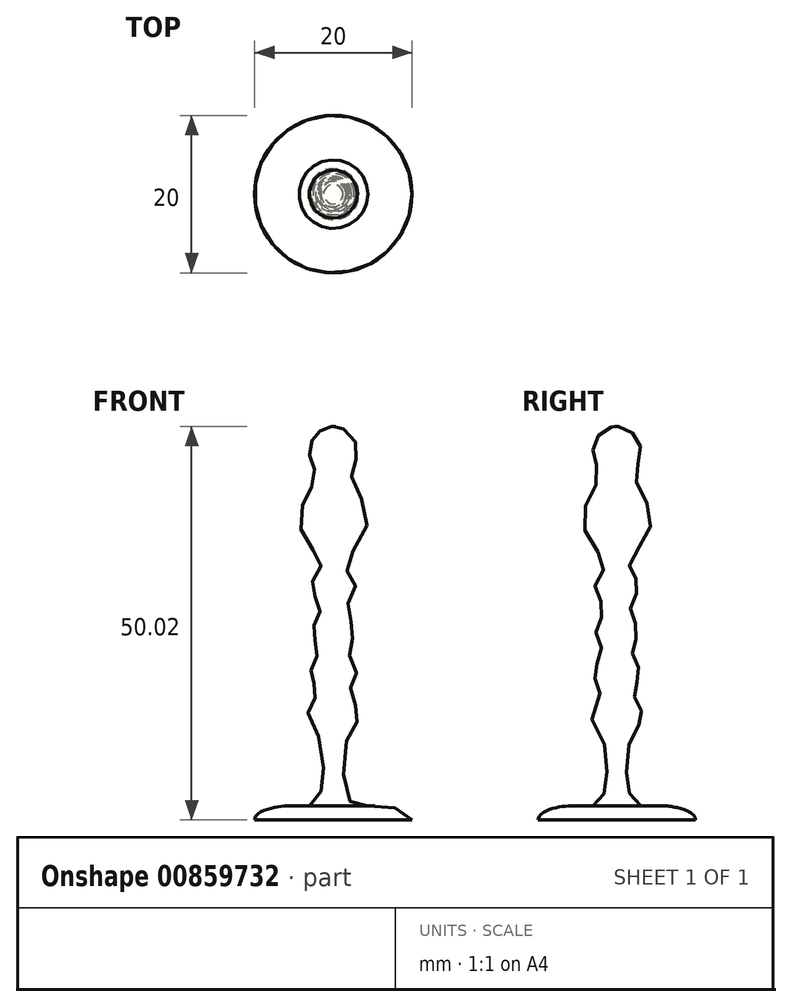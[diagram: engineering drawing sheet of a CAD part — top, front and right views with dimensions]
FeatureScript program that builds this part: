
annotation { "Feature Type Name" : "Feature", "Feature Type Description" : "" }
export const myFeature = defineFeature(function(context is Context, id is Id, definition is map)
    precondition{}
    {
        {
            var Q0;
            Q0=qCreatedBy(makeId("Front.planeOp"),FACE);
            var sketch = newSketch(context, id + "F0", { "sketchPlane" : qUnion([Q0])});
            skLineSegment(sketch, "E0", {"start": v(0, 0) * mm, "end": v(0, 50) * mm});
            skLineSegment(sketch, "E1", {"start": v(0, 0) * mm, "end": v(10, 0) * mm});
            skFitSpline(sketch, "E2", {"points": [v(10, 0) * mm, v(5.5, 1.83) * mm, v(2.11, 2.4) * mm, v(1.82, 10.43) * mm, v(3.26, 13.36) * mm, v(2.11, 16.34) * mm, v(2.91, 18.57) * mm, v(1.94, 21.44) * mm, v(2.63, 24.02) * mm, v(1.7, 26.83) * mm, v(2.8, 29.87) * mm, v(1.6, 32.22) * mm, v(4.35, 37.78) * mm, v(2.34, 43.51) * mm, v(2.97, 46.1) * mm, v(2.4, 48.79) * mm, v(0.45, 50) * mm, v(0, 50) * mm], "startDerivative": vector(0.85, 51.45) * mm, "endDerivative": vector(-16.22, -2.92) * mm});
            skSolve(sketch);
        }
        {
            var Q0;
            Q0=makeQuery(id+"F0.imprint","IMPRINT",FACE,{"disambiguationData":[TD([[makeQuery(id+"F0.imprint","IMPRINT",EDGE,{"derivedFrom":sQuery(id+"F0.wireOp",EDGE,"E0")}),-1.0]])]});
            var Q1;
            Q1=sQuery(id+"F0.wireOp",EDGE,"E0");
            revolve(context, id + "F1", {"surfaceOperationType" : NewSurfaceOperationType.NEW, "entities" : qUnion([Q0]), "axis" : qUnion([Q1]), "revolveType" : RevolveType.FULL});
        }
    });
